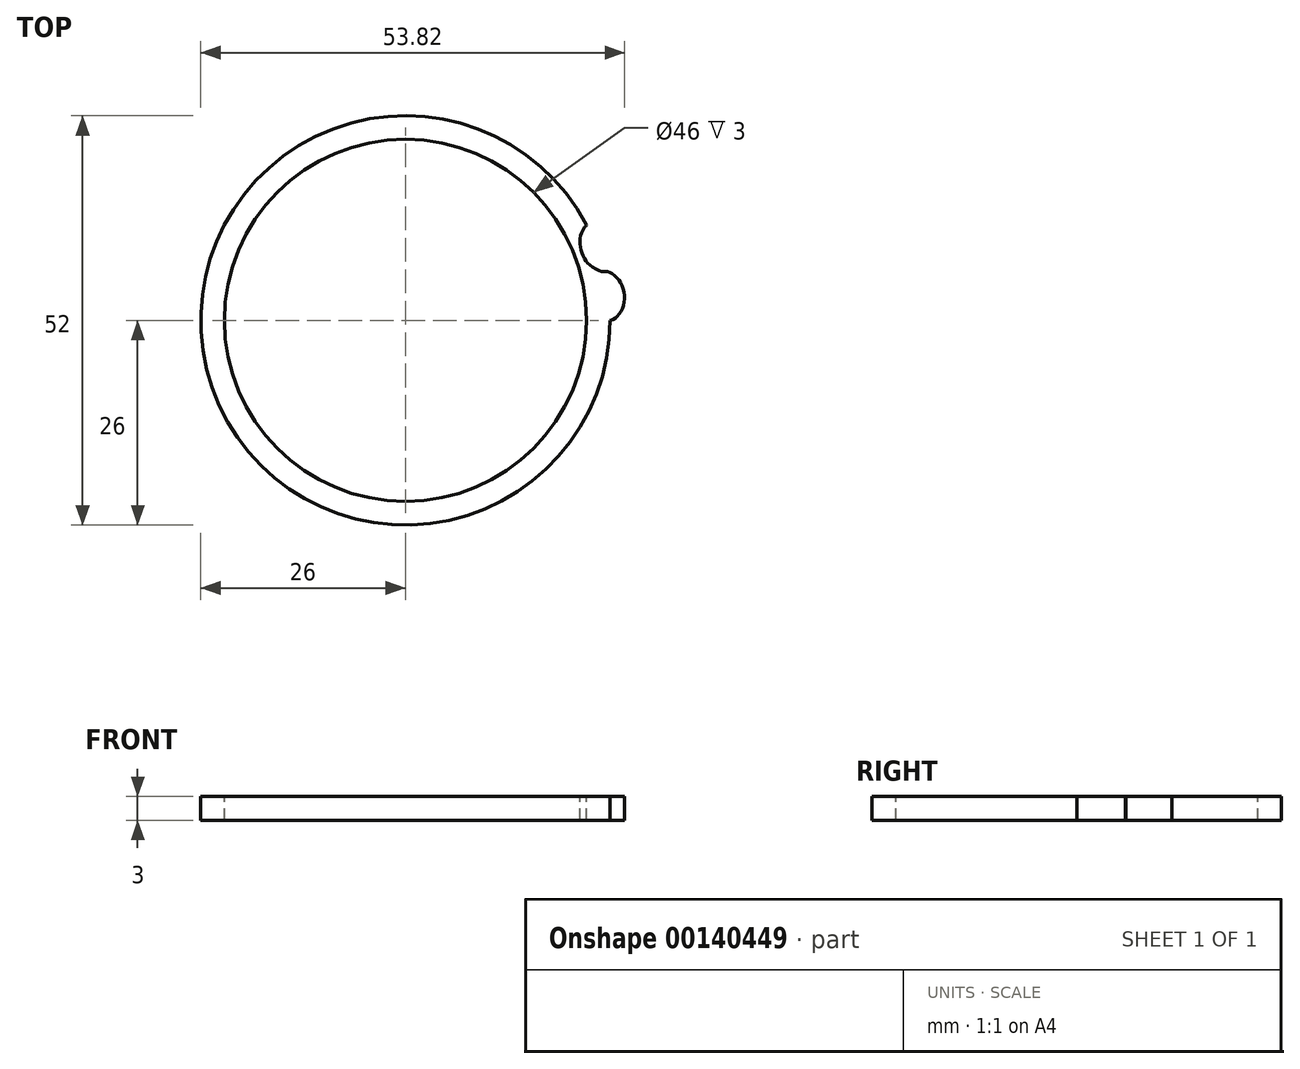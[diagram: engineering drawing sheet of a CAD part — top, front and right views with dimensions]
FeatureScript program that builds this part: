
annotation { "Feature Type Name" : "Feature", "Feature Type Description" : "" }
export const myFeature = defineFeature(function(context is Context, id is Id, definition is map)
    precondition{}
    {
        {
            assignVariable(context, id + "F0", {"name" : "t", "anyValue" : 3});
        }
        {
            var Q0;
            Q0=qCreatedBy(makeId("Top.planeOp"),FACE);
            var sketch = newSketch(context, id + "F1", { "sketchPlane" : qUnion([Q0])});
            skCircle(sketch, "E0", {"center": v(0, 0) * mm, "radius": 26 * mm});
            skSolve(sketch);
        }
        {
            var Q0;
            Q0=qSketchRegion(id+"F1",true);
            extrude(context, id + "F2", {"entities" : qUnion([Q0]), "depth" : (getVariable(context, 't')) * mm});
        }
        {
            var Q0;
            Q0=makeQuery(id+"F2.opExtrude","CAP_FACE",FACE,{"disambiguationData":[OSD([sQuery(id+"F1.wireOp",EDGE,"E0")])],"isStart":false});
            var sketch = newSketch(context, id + "F3", { "sketchPlane" : qUnion([Q0])});
            skLineSegment(sketch, "E1", {"start": v(0, 0) * mm, "end": v(25.24, 6.22) * mm, "construction": true});
            skLineSegment(sketch, "E2", {"start": v(25.24, 6.22) * mm, "end": v(27.19, 6.7) * mm, "construction": true});
            skPoint(sketch, "E3", {"position": v(26.22, 6.46) * mm});
            skCircle(sketch, "E4", {"center": v(26.22, 6.46) * mm, "radius": 1 * mm, "construction": true});
            skLineSegment(sketch, "E5", {"start": v(26, 0) * mm, "end": v(27, 0) * mm, "construction": true});
            skLineSegment(sketch, "E6", {"start": v(26.22, 6.46) * mm, "end": v(25.5, 5.77) * mm, "construction": true});
            skLineSegment(sketch, "E7", {"start": v(26.22, 6.46) * mm, "end": v(26.94, 7.15) * mm, "construction": true});
            skLineSegment(sketch, "E8", {"start": v(26.22, 6.46) * mm, "end": v(25.25, 6.74) * mm, "construction": true});
            skLineSegment(sketch, "E9", {"start": v(26.22, 6.46) * mm, "end": v(27.18, 6.18) * mm, "construction": true});
            skLineSegment(sketch, "E10", {"start": v(26.22, 6.46) * mm, "end": v(25.94, 5.5) * mm, "construction": true});
            skLineSegment(sketch, "E11", {"start": v(26.22, 6.46) * mm, "end": v(26.45, 5.5) * mm, "construction": true});
            skLineSegment(sketch, "E12", {"start": v(26.22, 6.46) * mm, "end": v(26.9, 5.74) * mm, "construction": true});
            skLineSegment(sketch, "E13", {"start": v(26.22, 6.46) * mm, "end": v(26.5, 7.42) * mm, "construction": true});
            skLineSegment(sketch, "E14", {"start": v(26.22, 6.46) * mm, "end": v(25.98, 7.43) * mm, "construction": true});
            skLineSegment(sketch, "E15", {"start": v(26.22, 6.46) * mm, "end": v(25.52, 7.18) * mm, "construction": true});
            skArc(sketch, "E16", {"start": v(27, 0) * mm, "mid": v(26.8, 3.25) * mm, "end": v(26.22, 6.46) * mm, "construction": true});
            skLineSegment(sketch, "E17", {"start": v(26.34, 5.93) * mm, "end": v(0, 0) * mm, "construction": true});
            skLineSegment(sketch, "E18", {"start": v(0, 0) * mm, "end": v(26.45, 5.4) * mm, "construction": true});
            skLineSegment(sketch, "E19", {"start": v(0, 0) * mm, "end": v(26.56, 4.87) * mm, "construction": true});
            skLineSegment(sketch, "E20", {"start": v(0, 0) * mm, "end": v(26.65, 4.33) * mm, "construction": true});
            skLineSegment(sketch, "E21", {"start": v(0, 0) * mm, "end": v(26.73, 3.8) * mm, "construction": true});
            skLineSegment(sketch, "E22", {"start": v(0, 0) * mm, "end": v(26.8, 3.25) * mm, "construction": true});
            skLineSegment(sketch, "E23", {"start": v(0, 0) * mm, "end": v(26.86, 2.71) * mm, "construction": true});
            skLineSegment(sketch, "E24", {"start": v(0, 0) * mm, "end": v(26.91, 2.17) * mm, "construction": true});
            skLineSegment(sketch, "E25", {"start": v(0, 0) * mm, "end": v(26.95, 1.63) * mm, "construction": true});
            skLineSegment(sketch, "E26", {"start": v(0, 0) * mm, "end": v(26.98, 1.09) * mm, "construction": true});
            skLineSegment(sketch, "E27", {"start": v(0, 0) * mm, "end": v(27, 0.54) * mm, "construction": true});
            skLineSegment(sketch, "E28", {"start": v(0, 0) * mm, "end": v(27, 0) * mm, "construction": true});
            skLineSegment(sketch, "E29", {"start": v(27, 0) * mm, "end": v(27.87, 0) * mm, "construction": true});
            skArc(sketch, "E30", {"start": v(25.25, 6.74) * mm, "mid": v(25.92, 3.4) * mm, "end": v(26.14, 0) * mm, "construction": true});
            skArc(sketch, "E31", {"start": v(25.52, 7.18) * mm, "mid": v(26.27, 3.63) * mm, "end": v(26.51, 0) * mm, "construction": true});
            skArc(sketch, "E32", {"start": v(25.98, 7.43) * mm, "mid": v(26.76, 3.75) * mm, "end": v(27.02, 0) * mm, "construction": true});
            skArc(sketch, "E33", {"start": v(26.5, 7.42) * mm, "mid": v(27.26, 3.75) * mm, "end": v(27.51, 0) * mm, "construction": true});
            skArc(sketch, "E34", {"start": v(26.94, 7.15) * mm, "mid": v(27.64, 3.6) * mm, "end": v(27.87, 0) * mm, "construction": true});
            skPoint(sketch, "E35", {"position": v(25.87, 5.83) * mm});
            skPoint(sketch, "E36", {"position": v(26.34, 5.93) * mm});
            skLineSegment(sketch, "E37", {"start": v(26.34, 5.93) * mm, "end": v(25.39, 6.23) * mm, "construction": true});
            skLineSegment(sketch, "E38", {"start": v(26.45, 5.4) * mm, "end": v(25.8, 6.15) * mm, "construction": true});
            skLineSegment(sketch, "E39", {"start": v(26.56, 4.87) * mm, "end": v(26.38, 5.85) * mm, "construction": true});
            skLineSegment(sketch, "E40", {"start": v(26.65, 4.33) * mm, "end": v(27, 5.27) * mm, "construction": true});
            skArc(sketch, "E41", {"start": v(27.19, 6.7) * mm, "mid": v(27.8, 3.38) * mm, "end": v(28, 0) * mm, "construction": true});
            skLineSegment(sketch, "E42", {"start": v(26.73, 3.8) * mm, "end": v(27.52, 4.41) * mm, "construction": true});
            skLineSegment(sketch, "E43", {"start": v(26.8, 3.25) * mm, "end": v(27.8, 3.38) * mm, "construction": true});
            skLineSegment(sketch, "E44", {"start": v(26.86, 2.71) * mm, "end": v(27.78, 2.3) * mm, "construction": true});
            skLineSegment(sketch, "E45", {"start": v(26.91, 2.17) * mm, "end": v(27.48, 1.35) * mm, "construction": true});
            skLineSegment(sketch, "E46", {"start": v(26.95, 1.63) * mm, "end": v(27.01, 0.63) * mm, "construction": true});
            skLineSegment(sketch, "E47", {"start": v(26.98, 1.09) * mm, "end": v(26.51, 0.2) * mm, "construction": true});
            skLineSegment(sketch, "E48", {"start": v(27, 0.54) * mm, "end": v(26.14, 0.03) * mm, "construction": true});
            skFitSpline(sketch, "E49", {"points": [v(25.24, 6.22) * mm, v(25.39, 6.23) * mm, v(25.8, 6.15) * mm, v(26.38, 5.85) * mm, v(27, 5.27) * mm, v(27.52, 4.41) * mm, v(27.8, 3.38) * mm, v(27.78, 2.3) * mm, v(27.48, 1.35) * mm, v(27.01, 0.63) * mm, v(26.51, 0.2) * mm, v(26.14, 0.03) * mm, v(26, 0) * mm], "startDerivative": vector(3.71, 0.92) * mm, "endDerivative": vector(-3.82, 0) * mm});
            skArc(sketch, "E50.0", {"start": v(26, 0) * mm, "mid": v(25.81, 3.13) * mm, "end": v(25.24, 6.22) * mm});
            skArc(sketch, "E51", {"start": v(25.24, 6.22) * mm, "mid": v(25.3, 5.97) * mm, "end": v(25.36, 5.71) * mm});
            skArc(sketch, "E52", {"start": v(25.36, 5.71) * mm, "mid": v(25.42, 5.46) * mm, "end": v(25.47, 5.2) * mm});
            skLineSegment(sketch, "E53", {"start": v(-26.57, -4.12) * mm, "end": v(2.46, 3.04) * mm, "construction": true});
            skLineSegment(sketch, "E54", {"start": v(2.46, 3.04) * mm, "end": v(4.4, 3.52) * mm, "construction": true});
            skPoint(sketch, "E55", {"position": v(3.43, 3.28) * mm});
            skCircle(sketch, "E56", {"center": v(3.43, 3.28) * mm, "radius": 1 * mm, "construction": true});
            skLineSegment(sketch, "E57", {"start": v(3.35, -4.12) * mm, "end": v(4.33, -4.12) * mm, "construction": true});
            skLineSegment(sketch, "E58", {"start": v(3.43, 3.28) * mm, "end": v(2.71, 2.59) * mm, "construction": true});
            skLineSegment(sketch, "E59", {"start": v(3.43, 3.28) * mm, "end": v(4.15, 3.97) * mm, "construction": true});
            skLineSegment(sketch, "E60", {"start": v(3.43, 3.28) * mm, "end": v(2.47, 3.56) * mm, "construction": true});
            skLineSegment(sketch, "E61", {"start": v(3.43, 3.28) * mm, "end": v(4.4, 3) * mm, "construction": true});
            skLineSegment(sketch, "E62", {"start": v(3.43, 3.28) * mm, "end": v(3.15, 2.32) * mm, "construction": true});
            skLineSegment(sketch, "E63", {"start": v(3.43, 3.28) * mm, "end": v(3.67, 2.3) * mm, "construction": true});
            skLineSegment(sketch, "E64", {"start": v(3.43, 3.28) * mm, "end": v(4.13, 2.56) * mm, "construction": true});
            skLineSegment(sketch, "E65", {"start": v(3.43, 3.28) * mm, "end": v(3.71, 4.24) * mm, "construction": true});
            skLineSegment(sketch, "E66", {"start": v(3.43, 3.28) * mm, "end": v(3.2, 4.25) * mm, "construction": true});
            skLineSegment(sketch, "E67", {"start": v(3.43, 3.28) * mm, "end": v(2.74, 4) * mm, "construction": true});
            skArc(sketch, "E68", {"start": v(4.33, -4.12) * mm, "mid": v(4.1, -0.4) * mm, "end": v(3.43, 3.28) * mm, "construction": true});
            skLineSegment(sketch, "E69", {"start": v(3.58, 2.67) * mm, "end": v(-26.57, -4.12) * mm, "construction": true});
            skLineSegment(sketch, "E70", {"start": v(-26.57, -4.12) * mm, "end": v(3.7, 2.07) * mm, "construction": true});
            skLineSegment(sketch, "E71", {"start": v(-26.57, -4.12) * mm, "end": v(3.82, 1.45) * mm, "construction": true});
            skLineSegment(sketch, "E72", {"start": v(-26.57, -4.12) * mm, "end": v(3.93, 0.84) * mm, "construction": true});
            skLineSegment(sketch, "E73", {"start": v(-26.57, -4.12) * mm, "end": v(4.02, 0.23) * mm, "construction": true});
            skLineSegment(sketch, "E74", {"start": v(-26.57, -4.12) * mm, "end": v(4.1, -0.4) * mm, "construction": true});
            skLineSegment(sketch, "E75", {"start": v(-26.57, -4.12) * mm, "end": v(4.17, -1) * mm, "construction": true});
            skLineSegment(sketch, "E76", {"start": v(-26.57, -4.12) * mm, "end": v(4.23, -1.63) * mm, "construction": true});
            skLineSegment(sketch, "E77", {"start": v(-26.57, -4.12) * mm, "end": v(4.27, -2.25) * mm, "construction": true});
            skLineSegment(sketch, "E78", {"start": v(-26.57, -4.12) * mm, "end": v(4.3, -2.87) * mm, "construction": true});
            skLineSegment(sketch, "E79", {"start": v(-26.57, -4.12) * mm, "end": v(4.32, -3.5) * mm, "construction": true});
            skLineSegment(sketch, "E80", {"start": v(-26.57, -4.12) * mm, "end": v(4.33, -4.12) * mm, "construction": true});
            skLineSegment(sketch, "E81", {"start": v(4.33, -4.12) * mm, "end": v(5.2, -4.12) * mm, "construction": true});
            skArc(sketch, "E82", {"start": v(2.47, 3.56) * mm, "mid": v(3.22, -0.25) * mm, "end": v(3.47, -4.12) * mm, "construction": true});
            skArc(sketch, "E83", {"start": v(2.74, 4) * mm, "mid": v(3.57, -0.02) * mm, "end": v(3.84, -4.12) * mm, "construction": true});
            skArc(sketch, "E84", {"start": v(3.2, 4.25) * mm, "mid": v(4.06, 0.1) * mm, "end": v(4.35, -4.12) * mm, "construction": true});
            skArc(sketch, "E85", {"start": v(3.71, 4.24) * mm, "mid": v(4.56, 0.1) * mm, "end": v(4.84, -4.12) * mm, "construction": true});
            skArc(sketch, "E86", {"start": v(4.15, 3.97) * mm, "mid": v(4.94, -0.04) * mm, "end": v(5.2, -4.12) * mm, "construction": true});
            skPoint(sketch, "E87", {"position": v(3.1, 2.57) * mm});
            skPoint(sketch, "E88", {"position": v(3.58, 2.67) * mm});
            skLineSegment(sketch, "E89", {"start": v(3.58, 2.67) * mm, "end": v(2.62, 2.97) * mm, "construction": true});
            skLineSegment(sketch, "E90", {"start": v(3.7, 2.07) * mm, "end": v(3.04, 2.81) * mm, "construction": true});
            skLineSegment(sketch, "E91", {"start": v(3.82, 1.45) * mm, "end": v(3.64, 2.44) * mm, "construction": true});
            skLineSegment(sketch, "E92", {"start": v(3.93, 0.84) * mm, "end": v(4.29, 1.78) * mm, "construction": true});
            skArc(sketch, "E93", {"start": v(4.4, 3.52) * mm, "mid": v(5.1, -0.27) * mm, "end": v(5.33, -4.12) * mm, "construction": true});
            skLineSegment(sketch, "E94", {"start": v(4.02, 0.23) * mm, "end": v(4.81, 0.84) * mm, "construction": true});
            skLineSegment(sketch, "E95", {"start": v(4.1, -0.4) * mm, "end": v(5.1, -0.27) * mm, "construction": true});
            skLineSegment(sketch, "E96", {"start": v(4.17, -1) * mm, "end": v(5.09, -1.42) * mm, "construction": true});
            skLineSegment(sketch, "E97", {"start": v(4.23, -1.63) * mm, "end": v(4.8, -2.45) * mm, "construction": true});
            skLineSegment(sketch, "E98", {"start": v(4.27, -2.25) * mm, "end": v(4.33, -3.25) * mm, "construction": true});
            skLineSegment(sketch, "E99", {"start": v(4.3, -2.87) * mm, "end": v(3.84, -3.76) * mm, "construction": true});
            skLineSegment(sketch, "E100", {"start": v(4.32, -3.5) * mm, "end": v(3.47, -4.01) * mm, "construction": true});
            skFitSpline(sketch, "E101", {"points": [v(2.46, 3.04) * mm, v(2.62, 2.97) * mm, v(3.04, 2.81) * mm, v(3.64, 2.44) * mm, v(4.29, 1.78) * mm, v(4.81, 0.84) * mm, v(5.1, -0.27) * mm, v(5.09, -1.42) * mm, v(4.8, -2.45) * mm, v(4.33, -3.25) * mm, v(3.84, -3.76) * mm, v(3.47, -4.01) * mm, v(3.35, -4.12) * mm], "startDerivative": vector(3.49, 0.86) * mm, "endDerivative": vector(-3.8, 0) * mm});
            skArc(sketch, "E102.0", {"start": v(3.35, -4.12) * mm, "mid": v(3.12, -0.51) * mm, "end": v(2.46, 3.04) * mm});
            skArc(sketch, "E103", {"start": v(2.46, 3.04) * mm, "mid": v(2.53, 2.75) * mm, "end": v(2.6, 2.45) * mm});
            skArc(sketch, "E104", {"start": v(2.6, 2.45) * mm, "mid": v(2.66, 2.16) * mm, "end": v(2.73, 1.87) * mm});
            skSolve(sketch);
        }
        {
            var Q0;
            Q0=qSketchRegion(id+"F3",true);
            var Q1;
            Q1=makeQuery(id+"F2.opExtrude","CAP_FACE",FACE,{"disambiguationData":[OSD([sQuery(id+"F1.wireOp",EDGE,"E0")])],"isStart":true});
            extrude(context, id + "F4", {"entities" : qUnion([Q0]), "operationType" : NewBodyOperationType.ADD, "endBound" : BoundingType.UP_TO_SURFACE, "oppositeDirection" : true, "endBoundEntityFace" : qUnion([Q1]), "depth" : 2.5 * mm});
        }
        {
            var Q0;
            {var subQ0=sQuery(id+"F3.wireOp",EDGE,"E50.0");Q0=makeQuery(id+"F3.imprint","IMPRINT",FACE,{"disambiguationData":[TD([[makeQuery(id+"F3.imprint","IMPRINT",EDGE,{"derivedFrom":subQ0}),1.0]])]});}
            var sketch = newSketch(context, id + "F5", { "sketchPlane" : qUnion([Q0])});
            skLineSegment(sketch, "E105.0", {"start": v(0, 0) * mm, "end": v(25.24, 6.22) * mm, "construction": true});
            skLineSegment(sketch, "E106.0.0", {"start": v(26, 0) * mm, "end": v(26, 0) * mm});
            skLineSegment(sketch, "E107", {"start": v(0, 0) * mm, "end": v(23.02, 12.08) * mm, "construction": true});
            skCircle(sketch, "E108", {"center": v(22.14, 11.62) * mm, "radius": 1 * mm, "construction": true});
            skArc(sketch, "E109", {"start": v(22.14, 11.62) * mm, "mid": v(23.38, 8.87) * mm, "end": v(24.27, 5.98) * mm, "construction": true});
            skLineSegment(sketch, "E110", {"start": v(22.14, 11.62) * mm, "end": v(22.6, 10.73) * mm, "construction": true});
            skArc(sketch, "E111", {"start": v(22.67, 12.46) * mm, "mid": v(24.1, 9.4) * mm, "end": v(25.12, 6.2) * mm, "construction": true});
            skArc(sketch, "E112", {"start": v(22.18, 12.62) * mm, "mid": v(23.7, 9.45) * mm, "end": v(24.77, 6.1) * mm, "construction": true});
            skArc(sketch, "E113", {"start": v(21.3, 12.15) * mm, "mid": v(22.77, 9.1) * mm, "end": v(23.8, 5.87) * mm, "construction": true});
            skArc(sketch, "E114", {"start": v(21.14, 11.66) * mm, "mid": v(22.48, 8.8) * mm, "end": v(23.44, 5.78) * mm, "construction": true});
            skArc(sketch, "E115", {"start": v(23.02, 12.08) * mm, "mid": v(23.14, 11.85) * mm, "end": v(23.26, 11.62) * mm});
            skLineSegment(sketch, "E116", {"start": v(23.26, 11.62) * mm, "end": v(0, 0) * mm, "construction": true});
            skArc(sketch, "E117", {"start": v(23.02, 12.08) * mm, "mid": v(24.31, 9.22) * mm, "end": v(25.24, 6.22) * mm});
            skLineSegment(sketch, "E118", {"start": v(0, 0) * mm, "end": v(23.49, 11.15) * mm, "construction": true});
            skLineSegment(sketch, "E119", {"start": v(0, 0) * mm, "end": v(23.7, 10.67) * mm, "construction": true});
            skLineSegment(sketch, "E120", {"start": v(0, 0) * mm, "end": v(23.92, 10.2) * mm, "construction": true});
            skLineSegment(sketch, "E121", {"start": v(0, 0) * mm, "end": v(24.12, 9.7) * mm, "construction": true});
            skLineSegment(sketch, "E122", {"start": v(0, 0) * mm, "end": v(24.31, 9.22) * mm, "construction": true});
            skLineSegment(sketch, "E123", {"start": v(0, 0) * mm, "end": v(24.5, 8.73) * mm, "construction": true});
            skLineSegment(sketch, "E124", {"start": v(0, 0) * mm, "end": v(24.66, 8.23) * mm, "construction": true});
            skLineSegment(sketch, "E125", {"start": v(24.82, 7.74) * mm, "end": v(0, 0) * mm, "construction": true});
            skLineSegment(sketch, "E126", {"start": v(0, 0) * mm, "end": v(24.97, 7.23) * mm, "construction": true});
            skLineSegment(sketch, "E127", {"start": v(0, 0) * mm, "end": v(25.11, 6.73) * mm, "construction": true});
            skLineSegment(sketch, "E128", {"start": v(22.37, 11.17) * mm, "end": v(22.92, 12) * mm, "construction": true});
            skLineSegment(sketch, "E129", {"start": v(22.59, 10.72) * mm, "end": v(22.67, 11.71) * mm, "construction": true});
            skArc(sketch, "E130", {"start": v(21.67, 12.5) * mm, "mid": v(23.21, 9.34) * mm, "end": v(24.3, 5.99) * mm, "construction": true});
            skLineSegment(sketch, "E131", {"start": v(22.8, 10.26) * mm, "end": v(22.39, 11.17) * mm, "construction": true});
            skLineSegment(sketch, "E132", {"start": v(23, 9.8) * mm, "end": v(22.2, 10.4) * mm, "construction": true});
            skLineSegment(sketch, "E133", {"start": v(23.2, 9.33) * mm, "end": v(22.2, 9.47) * mm, "construction": true});
            skLineSegment(sketch, "E134", {"start": v(23.38, 8.87) * mm, "end": v(22.44, 8.51) * mm, "construction": true});
            skArc(sketch, "E135", {"start": v(21.25, 11.15) * mm, "mid": v(22.44, 8.51) * mm, "end": v(23.3, 5.74) * mm, "construction": true});
            skLineSegment(sketch, "E136", {"start": v(23.55, 8.4) * mm, "end": v(22.9, 7.63) * mm, "construction": true});
            skLineSegment(sketch, "E137", {"start": v(23.71, 7.92) * mm, "end": v(23.51, 6.94) * mm, "construction": true});
            skLineSegment(sketch, "E138", {"start": v(24.01, 6.96) * mm, "end": v(24.73, 6.26) * mm, "construction": true});
            skLineSegment(sketch, "E139", {"start": v(24.15, 6.47) * mm, "end": v(25.11, 6.21) * mm, "construction": true});
            skFitSpline(sketch, "E140", {"points": [v(25.24, 6.22) * mm, v(25.11, 6.21) * mm, v(24.73, 6.26) * mm, v(23.51, 6.94) * mm, v(22.9, 7.63) * mm, v(22.44, 8.51) * mm, v(22.2, 9.47) * mm, v(22.2, 10.4) * mm, v(22.39, 11.17) * mm, v(22.67, 11.71) * mm, v(22.92, 12) * mm, v(23.02, 12.08) * mm], "startDerivative": vector(-3.52, -0.87) * mm, "endDerivative": vector(3.2, 1.68) * mm});
            skLineSegment(sketch, "E141", {"start": v(22.14, 11.62) * mm, "end": v(22.67, 12.46) * mm, "construction": true});
            skLineSegment(sketch, "E142", {"start": v(22.14, 11.62) * mm, "end": v(22.18, 12.62) * mm, "construction": true});
            skLineSegment(sketch, "E143", {"start": v(22.14, 11.62) * mm, "end": v(21.67, 12.5) * mm, "construction": true});
            skLineSegment(sketch, "E144", {"start": v(22.14, 11.62) * mm, "end": v(21.3, 12.15) * mm, "construction": true});
            skLineSegment(sketch, "E145", {"start": v(22.14, 11.62) * mm, "end": v(21.14, 11.66) * mm, "construction": true});
            skSolve(sketch);
        }
        {
            var Q0;
            Q0=qSketchRegion(id+"F5",true);
            extrude(context, id + "F6", {"entities" : qUnion([Q0]), "operationType" : NewBodyOperationType.REMOVE, "endBound" : BoundingType.THROUGH_ALL, "oppositeDirection" : true, "depth" : 25 * mm});
        }
        {
            var Q0;
            {var subQ0=sQuery(id+"F3.wireOp",EDGE,"E52");var subQ1=sQuery(id+"F3.wireOp",EDGE,"E51");var subQ2=sQuery(id+"F3.wireOp",EDGE,"E50.0");var subQ3=sQuery(id+"F3.wireOp",EDGE,"E49");Q0=makeQuery(id+"FYuu5osC36glpG0_1.29.F4.boolean.opBoolean","MERGE",FACE,{"derivedFrom":[makeQuery(id+"FYuu5osC36glpG0_1.28.F4.boolean.opBoolean","MERGE",FACE,{"derivedFrom":[makeQuery(id+"FYuu5osC36glpG0_1.27.F4.boolean.opBoolean","MERGE",FACE,{"derivedFrom":[makeQuery(id+"FYuu5osC36glpG0_1.26.F4.boolean.opBoolean","MERGE",FACE,{"derivedFrom":[makeQuery(id+"FYuu5osC36glpG0_1.25.F4.boolean.opBoolean","MERGE",FACE,{"derivedFrom":[makeQuery(id+"FYuu5osC36glpG0_1.24.F4.boolean.opBoolean","MERGE",FACE,{"derivedFrom":[makeQuery(id+"FYuu5osC36glpG0_1.23.F4.boolean.opBoolean","MERGE",FACE,{"derivedFrom":[makeQuery(id+"FYuu5osC36glpG0_1.22.F4.boolean.opBoolean","MERGE",FACE,{"derivedFrom":[makeQuery(id+"FYuu5osC36glpG0_1.21.F4.boolean.opBoolean","MERGE",FACE,{"derivedFrom":[makeQuery(id+"FYuu5osC36glpG0_1.20.F4.boolean.opBoolean","MERGE",FACE,{"derivedFrom":[makeQuery(id+"FYuu5osC36glpG0_1.19.F4.boolean.opBoolean","MERGE",FACE,{"derivedFrom":[makeQuery(id+"FYuu5osC36glpG0_1.18.F4.boolean.opBoolean","MERGE",FACE,{"derivedFrom":[makeQuery(id+"FYuu5osC36glpG0_1.17.F4.boolean.opBoolean","MERGE",FACE,{"derivedFrom":[makeQuery(id+"FYuu5osC36glpG0_1.16.F4.boolean.opBoolean","MERGE",FACE,{"derivedFrom":[makeQuery(id+"FYuu5osC36glpG0_1.15.F4.boolean.opBoolean","MERGE",FACE,{"derivedFrom":[makeQuery(id+"FYuu5osC36glpG0_1.14.F4.boolean.opBoolean","MERGE",FACE,{"derivedFrom":[makeQuery(id+"FYuu5osC36glpG0_1.13.F4.boolean.opBoolean","MERGE",FACE,{"derivedFrom":[makeQuery(id+"FYuu5osC36glpG0_1.12.F4.boolean.opBoolean","MERGE",FACE,{"derivedFrom":[makeQuery(id+"FYuu5osC36glpG0_1.11.F4.boolean.opBoolean","MERGE",FACE,{"derivedFrom":[makeQuery(id+"FYuu5osC36glpG0_1.10.F4.boolean.opBoolean","MERGE",FACE,{"derivedFrom":[makeQuery(id+"FYuu5osC36glpG0_1.9.F4.boolean.opBoolean","MERGE",FACE,{"derivedFrom":[makeQuery(id+"FYuu5osC36glpG0_1.8.F4.boolean.opBoolean","MERGE",FACE,{"derivedFrom":[makeQuery(id+"FYuu5osC36glpG0_1.7.F4.boolean.opBoolean","MERGE",FACE,{"derivedFrom":[makeQuery(id+"FYuu5osC36glpG0_1.6.F4.boolean.opBoolean","MERGE",FACE,{"derivedFrom":[makeQuery(id+"FYuu5osC36glpG0_1.5.F4.boolean.opBoolean","MERGE",FACE,{"derivedFrom":[makeQuery(id+"FYuu5osC36glpG0_1.4.F4.boolean.opBoolean","MERGE",FACE,{"derivedFrom":[makeQuery(id+"FYuu5osC36glpG0_1.3.F4.boolean.opBoolean","MERGE",FACE,{"derivedFrom":[makeQuery(id+"FYuu5osC36glpG0_1.2.F4.boolean.opBoolean","MERGE",FACE,{"derivedFrom":[makeQuery(id+"FYuu5osC36glpG0_1.1.F4.boolean.opBoolean","MERGE",FACE,{"derivedFrom":[makeQuery(id+"F4.boolean.opBoolean","MERGE",FACE,{"derivedFrom":[makeQuery(id+"F2.opExtrude","CAP_FACE",FACE,{"disambiguationData":[OSD([sQuery(id+"F1.wireOp",EDGE,"E0")])],"isStart":false}),makeQuery(id+"F4.opExtrude","CAP_FACE",FACE,{"disambiguationData":[OSD([subQ3,subQ2,subQ1,subQ0])],"isStart":true})]}),makeQuery(id+"FYuu5osC36glpG0_1.1.F4.opExtrude","CAP_FACE",FACE,{"disambiguationData":[OSD([subQ3,subQ2,subQ1,subQ0])],"isStart":true})]}),makeQuery(id+"FYuu5osC36glpG0_1.2.F4.opExtrude","CAP_FACE",FACE,{"disambiguationData":[OSD([subQ3,subQ2,subQ1,subQ0])],"isStart":true})]}),makeQuery(id+"FYuu5osC36glpG0_1.3.F4.opExtrude","CAP_FACE",FACE,{"disambiguationData":[OSD([subQ3,subQ2,subQ1,subQ0])],"isStart":true})]}),makeQuery(id+"FYuu5osC36glpG0_1.4.F4.opExtrude","CAP_FACE",FACE,{"disambiguationData":[OSD([subQ3,subQ2,subQ1,subQ0])],"isStart":true})]}),makeQuery(id+"FYuu5osC36glpG0_1.5.F4.opExtrude","CAP_FACE",FACE,{"disambiguationData":[OSD([subQ3,subQ2,subQ1,subQ0])],"isStart":true})]}),makeQuery(id+"FYuu5osC36glpG0_1.6.F4.opExtrude","CAP_FACE",FACE,{"disambiguationData":[OSD([subQ3,subQ2,subQ1,subQ0])],"isStart":true})]}),makeQuery(id+"FYuu5osC36glpG0_1.7.F4.opExtrude","CAP_FACE",FACE,{"disambiguationData":[OSD([subQ3,subQ2,subQ1,subQ0])],"isStart":true})]}),makeQuery(id+"FYuu5osC36glpG0_1.8.F4.opExtrude","CAP_FACE",FACE,{"disambiguationData":[OSD([subQ3,subQ2,subQ1,subQ0])],"isStart":true})]}),makeQuery(id+"FYuu5osC36glpG0_1.9.F4.opExtrude","CAP_FACE",FACE,{"disambiguationData":[OSD([subQ3,subQ2,subQ1,subQ0])],"isStart":true})]}),makeQuery(id+"FYuu5osC36glpG0_1.10.F4.opExtrude","CAP_FACE",FACE,{"disambiguationData":[OSD([subQ3,subQ2,subQ1,subQ0])],"isStart":true})]}),makeQuery(id+"FYuu5osC36glpG0_1.11.F4.opExtrude","CAP_FACE",FACE,{"disambiguationData":[OSD([subQ3,subQ2,subQ1,subQ0])],"isStart":true})]}),makeQuery(id+"FYuu5osC36glpG0_1.12.F4.opExtrude","CAP_FACE",FACE,{"disambiguationData":[OSD([subQ3,subQ2,subQ1,subQ0])],"isStart":true})]}),makeQuery(id+"FYuu5osC36glpG0_1.13.F4.opExtrude","CAP_FACE",FACE,{"disambiguationData":[OSD([subQ3,subQ2,subQ1,subQ0])],"isStart":true})]}),makeQuery(id+"FYuu5osC36glpG0_1.14.F4.opExtrude","CAP_FACE",FACE,{"disambiguationData":[OSD([subQ3,subQ2,subQ1,subQ0])],"isStart":true})]}),makeQuery(id+"FYuu5osC36glpG0_1.15.F4.opExtrude","CAP_FACE",FACE,{"disambiguationData":[OSD([subQ3,subQ2,subQ1,subQ0])],"isStart":true})]}),makeQuery(id+"FYuu5osC36glpG0_1.16.F4.opExtrude","CAP_FACE",FACE,{"disambiguationData":[OSD([subQ3,subQ2,subQ1,subQ0])],"isStart":true})]}),makeQuery(id+"FYuu5osC36glpG0_1.17.F4.opExtrude","CAP_FACE",FACE,{"disambiguationData":[OSD([subQ3,subQ2,subQ1,subQ0])],"isStart":true})]}),makeQuery(id+"FYuu5osC36glpG0_1.18.F4.opExtrude","CAP_FACE",FACE,{"disambiguationData":[OSD([subQ3,subQ2,subQ1,subQ0])],"isStart":true})]}),makeQuery(id+"FYuu5osC36glpG0_1.19.F4.opExtrude","CAP_FACE",FACE,{"disambiguationData":[OSD([subQ3,subQ2,subQ1,subQ0])],"isStart":true})]}),makeQuery(id+"FYuu5osC36glpG0_1.20.F4.opExtrude","CAP_FACE",FACE,{"disambiguationData":[OSD([subQ3,subQ2,subQ1,subQ0])],"isStart":true})]}),makeQuery(id+"FYuu5osC36glpG0_1.21.F4.opExtrude","CAP_FACE",FACE,{"disambiguationData":[OSD([subQ3,subQ2,subQ1,subQ0])],"isStart":true})]}),makeQuery(id+"FYuu5osC36glpG0_1.22.F4.opExtrude","CAP_FACE",FACE,{"disambiguationData":[OSD([subQ3,subQ2,subQ1,subQ0])],"isStart":true})]}),makeQuery(id+"FYuu5osC36glpG0_1.23.F4.opExtrude","CAP_FACE",FACE,{"disambiguationData":[OSD([subQ3,subQ2,subQ1,subQ0])],"isStart":true})]}),makeQuery(id+"FYuu5osC36glpG0_1.24.F4.opExtrude","CAP_FACE",FACE,{"disambiguationData":[OSD([subQ3,subQ2,subQ1,subQ0])],"isStart":true})]}),makeQuery(id+"FYuu5osC36glpG0_1.25.F4.opExtrude","CAP_FACE",FACE,{"disambiguationData":[OSD([subQ3,subQ2,subQ1,subQ0])],"isStart":true})]}),makeQuery(id+"FYuu5osC36glpG0_1.26.F4.opExtrude","CAP_FACE",FACE,{"disambiguationData":[OSD([subQ3,subQ2,subQ1,subQ0])],"isStart":true})]}),makeQuery(id+"FYuu5osC36glpG0_1.27.F4.opExtrude","CAP_FACE",FACE,{"disambiguationData":[OSD([subQ3,subQ2,subQ1,subQ0])],"isStart":true})]}),makeQuery(id+"FYuu5osC36glpG0_1.28.F4.opExtrude","CAP_FACE",FACE,{"disambiguationData":[OSD([subQ3,subQ2,subQ1,subQ0])],"isStart":true})]}),makeQuery(id+"FYuu5osC36glpG0_1.29.F4.opExtrude","CAP_FACE",FACE,{"disambiguationData":[OSD([subQ3,subQ2,subQ1,subQ0])],"isStart":true})]});}
            var sketch = newSketch(context, id + "F7", { "sketchPlane" : qUnion([Q0])});
            skCircle(sketch, "E146", {"center": v(0, 0) * mm, "radius": 23 * mm});
            skSolve(sketch);
        }
        {
            var Q0;
            Q0=qSketchRegion(id+"F7",true);
            extrude(context, id + "F8", {"entities" : qUnion([Q0]), "operationType" : NewBodyOperationType.REMOVE, "endBound" : BoundingType.THROUGH_ALL, "oppositeDirection" : true, "depth" : 25 * mm});
        }
    });
